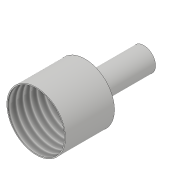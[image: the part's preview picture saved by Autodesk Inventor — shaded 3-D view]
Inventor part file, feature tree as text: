
AUTODESK INVENTOR PART (.ipt)
format: ipt  version: 2019 (Build 230136000, 136)  size: 116,736 bytes
history: native  units: in
note: dims shown in document units (in); Inventor stores cm internally (conversion verified against a paired STEP export)
features: sketch x7, extrude x6, thread x1
ambient origin geometry x8: Origin, YZ Plane, XZ Plane, XY Plane, X Axis, Y Axis, Z Axis, Center Point
bodies: Solid1 (feature_tree)
feature tree (14):
  extrude  "Extrusion1"  Depth=0.9843in TaperAngle=0.0deg
  extrude  "Extrusion2"  Depth=0.8661in TaperAngle=0.0deg
  extrude  "Extrusion3"  Depth=0.3937in TaperAngle=0.0deg
  thread  "Thread1"  [1 undecoded]
  extrude  "Extrusion4"  Depth=1.1811in
  sketch  "Sketch5"  dims[d15=0.0433in d16=0.3543in d17=0.1772in d18=0.0in d19=0.0in]
  extrude  "Extrusion5"  Depth=0.3543in TaperAngle=0.0deg
  extrude  "Extrusion6"  Depth=0.4724in
  sketch  "Sketch1"  dims[d0=1.1811in d1=0.9843in d2=0.0in]
  sketch  "Sketch2"  dims[d3=1.1417in d4=0.8661in d5=0.0in]
  sketch  "Sketch3"  dims[d6=1.1417in d7=0.8661in d8=0.0in d9=0.3937in d10=0.0in]
  sketch  "Sketch4"  dims[d12=1.1811in d13=0.0in d14=0.1575in]
  sketch  "Sketch6"  dims[d22=0.2756in d23=0.0in d24=0.4724in]
  sketch  "Sketch7"  dims[d25=0.3937in]
note: 1 required parameter value undecoded (feature->parameter linkage not recoverable at this tier; creation-order binding heuristic only, values carry confidence <= 0.55)
